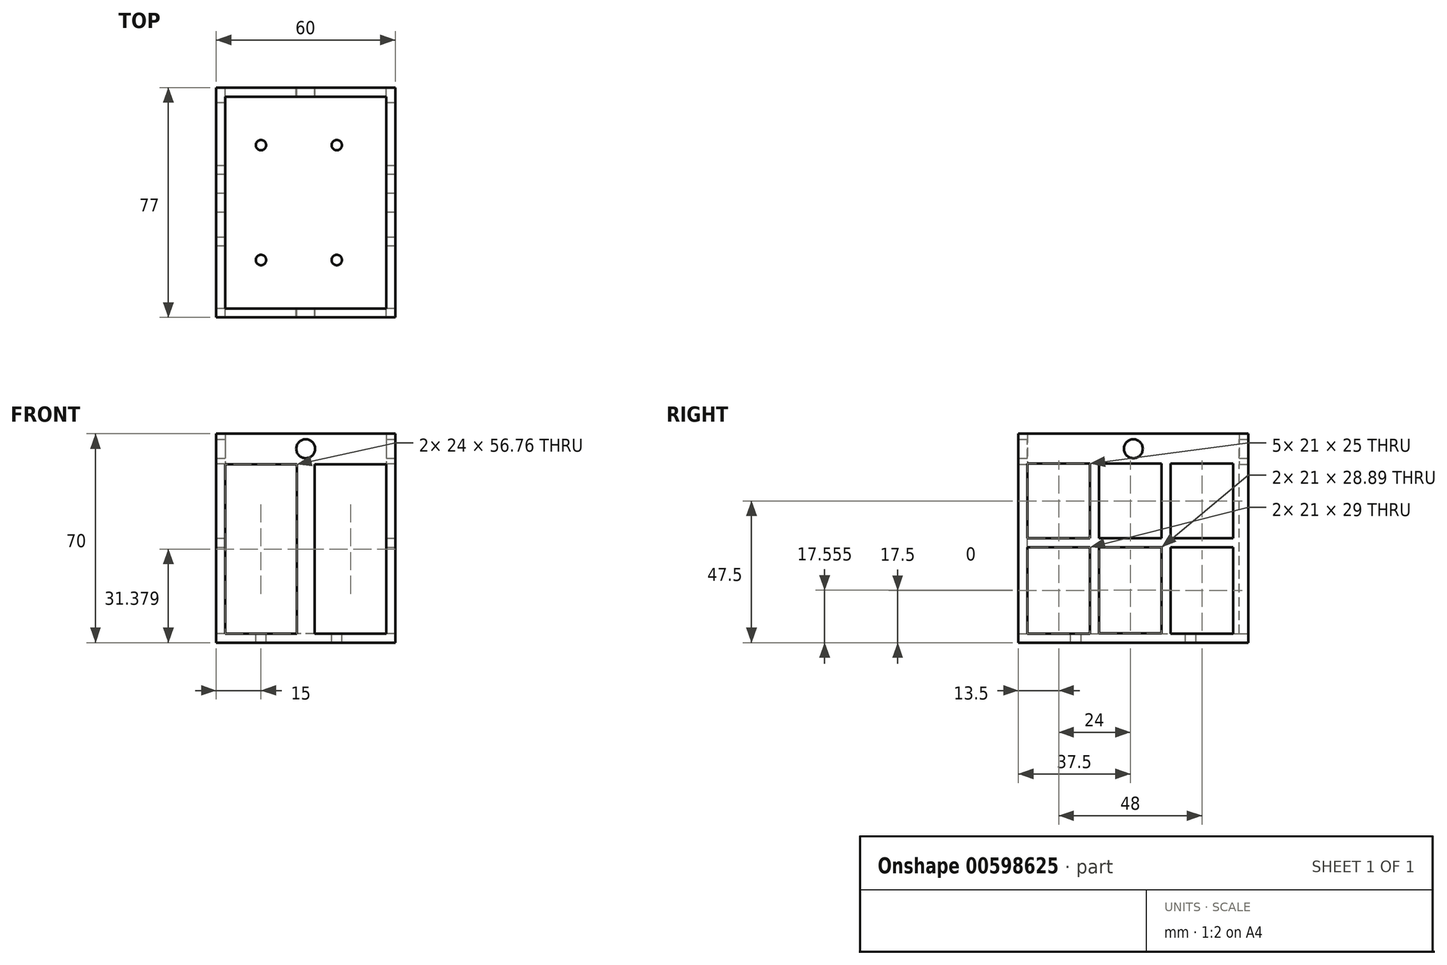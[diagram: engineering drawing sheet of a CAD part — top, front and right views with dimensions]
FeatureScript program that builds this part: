
annotation { "Feature Type Name" : "Feature", "Feature Type Description" : "" }
export const myFeature = defineFeature(function(context is Context, id is Id, definition is map)
    precondition{}
    {
        {
            var Q0;
            Q0=qCreatedBy(makeId("Top.planeOp"),FACE);
            var sketch = newSketch(context, id + "F0", { "sketchPlane" : qUnion([Q0])});
            skLineSegment(sketch, "E0.bottom", {"start": v(30, -38.5) * mm, "end": v(-30, -38.5) * mm});
            skLineSegment(sketch, "E0.top", {"start": v(30, 38.5) * mm, "end": v(-30, 38.5) * mm});
            skLineSegment(sketch, "E0.left", {"start": v(30, -38.5) * mm, "end": v(30, 38.5) * mm});
            skLineSegment(sketch, "E0.right", {"start": v(-30, -38.5) * mm, "end": v(-30, 38.5) * mm});
            skPoint(sketch, "E0.middle", {"position": v(0, 0) * mm});
            skSolve(sketch);
        }
        {
            var Q0;
            Q0=makeQuery(id+"F0.imprint","IMPRINT",FACE,{"disambiguationData":[TD([[makeQuery(id+"F0.imprint","IMPRINT",EDGE,{"derivedFrom":sQuery(id+"F0.wireOp",EDGE,"E0.bottom")}),-1.0]])]});
            extrude(context, id + "F1", {"entities" : qUnion([Q0]), "depth" : 70 * mm, "offsetDistance" : 25.4 * mm});
        }
        {
            var Q0;
            Q0=makeQuery(id+"F1.opExtrude","CAP_FACE",FACE,{"disambiguationData":[OSD([sQuery(id+"F0.wireOp",EDGE,"E0.bottom"),sQuery(id+"F0.wireOp",EDGE,"E0.top"),sQuery(id+"F0.wireOp",EDGE,"E0.left"),sQuery(id+"F0.wireOp",EDGE,"E0.right")])],"isStart":false});
            shell(context, id + "F2", {"entities" : qUnion([Q0]), "thickness" : 3 * mm});
        }
        {
            var Q0;
            Q0=makeQuery(id+"F1.opExtrude","SWEPT_FACE",FACE,{"disambiguationData":[OSD([sQuery(id+"F0.wireOp",EDGE,"E0.left")])]});
            var sketch = newSketch(context, id + "F3", { "sketchPlane" : qUnion([Q0])});
            skLineSegment(sketch, "E1.left", {"start": v(-35.5, 60) * mm, "end": v(-35.5, 35) * mm});
            skLineSegment(sketch, "E2.0", {"start": v(-38.5, 70) * mm, "end": v(38.5, 70) * mm});
            skLineSegment(sketch, "E3.0", {"start": v(-38.5, 70) * mm, "end": v(-38.5, 0) * mm});
            skLineSegment(sketch, "E4.0", {"start": v(38.5, 70) * mm, "end": v(38.5, 0) * mm});
            skLineSegment(sketch, "E5.left", {"start": v(-35.5, 32) * mm, "end": v(-35.5, 3) * mm});
            skCircle(sketch, "E6", {"center": v(0, 65) * mm, "radius": 3.18 * mm});
            skPoint(sketch, "E6.centerSnap0", {"position": v(0, 70) * mm});
            skLineSegment(sketch, "E7", {"start": v(-35.5, 60) * mm, "end": v(-14.5, 60) * mm});
            skLineSegment(sketch, "E8", {"start": v(-14.5, 60) * mm, "end": v(-14.5, 35) * mm});
            skLineSegment(sketch, "E9", {"start": v(-14.5, 35) * mm, "end": v(-35.5, 35) * mm});
            skLineSegment(sketch, "E10.bottom", {"start": v(-11.5, 60) * mm, "end": v(9.5, 60) * mm});
            skLineSegment(sketch, "E10.top", {"start": v(-11.5, 35) * mm, "end": v(9.5, 35) * mm});
            skLineSegment(sketch, "E10.left", {"start": v(-11.5, 60) * mm, "end": v(-11.5, 35) * mm});
            skLineSegment(sketch, "E10.right", {"start": v(9.5, 60) * mm, "end": v(9.5, 35) * mm});
            skLineSegment(sketch, "E11.bottom", {"start": v(12.5, 60) * mm, "end": v(33.5, 60) * mm});
            skLineSegment(sketch, "E11.top", {"start": v(12.5, 35) * mm, "end": v(33.5, 35) * mm});
            skLineSegment(sketch, "E11.left", {"start": v(12.5, 60) * mm, "end": v(12.5, 35) * mm});
            skLineSegment(sketch, "E11.right", {"start": v(33.5, 60) * mm, "end": v(33.5, 35) * mm});
            skLineSegment(sketch, "E12", {"start": v(-35.5, 32) * mm, "end": v(-14.5, 32) * mm});
            skLineSegment(sketch, "E13", {"start": v(-14.5, 32) * mm, "end": v(-14.5, 3) * mm});
            skLineSegment(sketch, "E14", {"start": v(-14.5, 3) * mm, "end": v(-35.5, 3) * mm});
            skLineSegment(sketch, "E15.bottom", {"start": v(-11.5, 32) * mm, "end": v(9.5, 32) * mm});
            skLineSegment(sketch, "E15.top", {"start": v(-11.5, 3.11) * mm, "end": v(9.5, 3.11) * mm});
            skLineSegment(sketch, "E15.left", {"start": v(-11.5, 32) * mm, "end": v(-11.5, 3.11) * mm});
            skLineSegment(sketch, "E15.right", {"start": v(9.5, 32) * mm, "end": v(9.5, 3.11) * mm});
            skPoint(sketch, "E16.oppositeSnap0", {"position": v(-25, 3) * mm});
            skLineSegment(sketch, "E16.bottom", {"start": v(12.5, 32) * mm, "end": v(33.5, 32) * mm});
            skLineSegment(sketch, "E16.top", {"start": v(12.5, 3) * mm, "end": v(33.5, 3) * mm});
            skLineSegment(sketch, "E16.left", {"start": v(12.5, 32) * mm, "end": v(12.5, 3) * mm});
            skLineSegment(sketch, "E16.right", {"start": v(33.5, 32) * mm, "end": v(33.5, 3) * mm});
            skSolve(sketch);
        }
        {
            var Q0;
            Q0=makeQuery(id+"F3.imprint","IMPRINT",FACE,{"disambiguationData":[TD([[makeQuery(id+"F3.imprint","IMPRINT",EDGE,{"derivedFrom":sQuery(id+"F3.wireOp",EDGE,"E1.bottom")}),-1.0]])]});
            var Q1;
            Q1=makeQuery(id+"F3.imprint","IMPRINT",FACE,{"disambiguationData":[TD([[makeQuery(id+"F3.imprint","IMPRINT",EDGE,{"derivedFrom":sQuery(id+"F3.wireOp",EDGE,"7c4a7869-6593-47a0-92b5-f3390c8ad75b.1.0.0")}),1.0]])]});
            var Q2;
            Q2=makeQuery(id+"F3.imprint","IMPRINT",FACE,{"disambiguationData":[TD([[makeQuery(id+"F3.imprint","IMPRINT",EDGE,{"derivedFrom":sQuery(id+"F3.wireOp",EDGE,"E1.left")}),1.0]])]});
            var Q3;
            Q3=makeQuery(id+"F3.imprint","IMPRINT",FACE,{"disambiguationData":[TD([[makeQuery(id+"F3.imprint","IMPRINT",EDGE,{"derivedFrom":sQuery(id+"F3.wireOp",EDGE,"E10.bottom")}),-1.0]])]});
            var Q4;
            Q4=makeQuery(id+"F3.imprint","IMPRINT",FACE,{"disambiguationData":[TD([[makeQuery(id+"F3.imprint","IMPRINT",EDGE,{"derivedFrom":sQuery(id+"F3.wireOp",EDGE,"E11.bottom")}),-1.0]])]});
            var Q5;
            Q5=makeQuery(id+"F3.imprint","IMPRINT",FACE,{"disambiguationData":[TD([[makeQuery(id+"F3.imprint","IMPRINT",EDGE,{"derivedFrom":sQuery(id+"F3.wireOp",EDGE,"E5.left")}),1.0]])]});
            var Q6;
            Q6=makeQuery(id+"F3.imprint","IMPRINT",FACE,{"disambiguationData":[TD([[makeQuery(id+"F3.imprint","IMPRINT",EDGE,{"derivedFrom":sQuery(id+"F3.wireOp",EDGE,"E15.bottom")}),-1.0]])]});
            var Q7;
            Q7=makeQuery(id+"F3.imprint","IMPRINT",FACE,{"disambiguationData":[TD([[makeQuery(id+"F3.imprint","IMPRINT",EDGE,{"derivedFrom":sQuery(id+"F3.wireOp",EDGE,"E16.bottom")}),-1.0]])]});
            extrude(context, id + "F4", {"entities" : qUnion([Q0, Q1, Q2, Q3, Q4, Q5, Q6, Q7]), "operationType" : NewBodyOperationType.REMOVE, "endBound" : BoundingType.THROUGH_ALL, "oppositeDirection" : true, "depth" : 25.4 * mm, "offsetDistance" : 25.4 * mm});
        }
        {
            var Q0;
            Q0=makeQuery(id+"F2.opShell","OFFSET_FACE",FACE,{"disambiguationData":[OSD([sQuery(id+"F0.wireOp",EDGE,"E0.bottom"),sQuery(id+"F0.wireOp",EDGE,"E0.top"),sQuery(id+"F0.wireOp",EDGE,"E0.left"),sQuery(id+"F0.wireOp",EDGE,"E0.right")])]});
            var sketch = newSketch(context, id + "F5", { "sketchPlane" : qUnion([Q0])});
            skPoint(sketch, "E17.0", {"position": v(-30, -38.5) * mm});
            skLineSegment(sketch, "E18", {"start": v(-30, -38.5) * mm, "end": v(0, 0) * mm, "construction": true});
            skPoint(sketch, "E19.0", {"position": v(-30, 0) * mm});
            skPoint(sketch, "E20.0", {"position": v(0, -38.5) * mm});
            skLineSegment(sketch, "E21", {"start": v(-30, 0) * mm, "end": v(0, -38.5) * mm, "construction": true});
            skCircle(sketch, "E22", {"center": v(-15, -19.25) * mm, "radius": 1.75 * mm});
            skCircle(sketch, "E23.0.1.0", {"center": v(-15, 19.25) * mm, "radius": 1.75 * mm});
            skCircle(sketch, "E23.1.0.0", {"center": v(10.4, -19.25) * mm, "radius": 1.75 * mm});
            skCircle(sketch, "E23.1.1.0", {"center": v(10.4, 19.25) * mm, "radius": 1.75 * mm});
            skLineSegment(sketch, "E23.direction1", {"start": v(-15, -19.25) * mm, "end": v(10.4, -19.25) * mm, "construction": true});
            skLineSegment(sketch, "E23.direction2", {"start": v(-15, -19.25) * mm, "end": v(-15, 19.25) * mm, "construction": true});
            skSolve(sketch);
        }
        {
            var Q0;
            Q0=makeQuery(id+"F5.imprint","IMPRINT",FACE,{"disambiguationData":[TD([[makeQuery(id+"F5.imprint","IMPRINT",EDGE,{"derivedFrom":sQuery(id+"F5.wireOp",EDGE,"E22")}),1.0]])]});
            var Q1;
            Q1=makeQuery(id+"F5.imprint","IMPRINT",FACE,{"disambiguationData":[TD([[makeQuery(id+"F5.imprint","IMPRINT",EDGE,{"derivedFrom":sQuery(id+"F5.wireOp",EDGE,"E23.1.0.0")}),1.0]])]});
            var Q2;
            Q2=makeQuery(id+"F5.imprint","IMPRINT",FACE,{"disambiguationData":[TD([[makeQuery(id+"F5.imprint","IMPRINT",EDGE,{"derivedFrom":sQuery(id+"F5.wireOp",EDGE,"E23.0.1.0")}),1.0]])]});
            var Q3;
            Q3=makeQuery(id+"F5.imprint","IMPRINT",FACE,{"disambiguationData":[TD([[makeQuery(id+"F5.imprint","IMPRINT",EDGE,{"derivedFrom":sQuery(id+"F5.wireOp",EDGE,"E23.1.1.0")}),1.0]])]});
            extrude(context, id + "F6", {"entities" : qUnion([Q0, Q1, Q2, Q3]), "operationType" : NewBodyOperationType.REMOVE, "endBound" : BoundingType.THROUGH_ALL, "oppositeDirection" : true, "depth" : 25 * mm, "offsetDistance" : 25 * mm});
        }
        {
            var Q0;
            Q0=makeQuery(id+"F3.imprint","IMPRINT",FACE,{"disambiguationData":[TD([[makeQuery(id+"F3.imprint","IMPRINT",EDGE,{"derivedFrom":sQuery(id+"F3.wireOp",EDGE,"E5.bottom")}),-1.0]])]});
            var Q1;
            Q1=makeQuery(id+"F3.imprint","IMPRINT",FACE,{"disambiguationData":[TD([[makeQuery(id+"F3.imprint","IMPRINT",EDGE,{"derivedFrom":sQuery(id+"F3.wireOp",EDGE,"E6")}),1.0]])]});
            extrude(context, id + "F7", {"entities" : qUnion([Q0, Q1]), "operationType" : NewBodyOperationType.REMOVE, "endBound" : BoundingType.THROUGH_ALL, "oppositeDirection" : true, "depth" : 25 * mm, "offsetDistance" : 25 * mm});
        }
        {
            var Q0;
            Q0=makeQuery(id+"F1.opExtrude","SWEPT_FACE",FACE,{"disambiguationData":[OSD([sQuery(id+"F0.wireOp",EDGE,"E0.top")])]});
            var sketch = newSketch(context, id + "F8", { "sketchPlane" : qUnion([Q0])});
            skCircle(sketch, "E24", {"center": v(0, 65) * mm, "radius": 3.18 * mm});
            skPoint(sketch, "E24.centerSnap0", {"position": v(0, 70) * mm});
            skLineSegment(sketch, "E25.bottom", {"start": v(-27, 59.76) * mm, "end": v(-3, 59.76) * mm});
            skLineSegment(sketch, "E25.top", {"start": v(-27, 3) * mm, "end": v(-3, 3) * mm});
            skLineSegment(sketch, "E25.left", {"start": v(-27, 59.76) * mm, "end": v(-27, 3) * mm});
            skLineSegment(sketch, "E25.right", {"start": v(-3, 59.76) * mm, "end": v(-3, 3) * mm});
            skLineSegment(sketch, "E26.bottom", {"start": v(3, 59.76) * mm, "end": v(27, 59.76) * mm});
            skLineSegment(sketch, "E26.top", {"start": v(3, 3) * mm, "end": v(27, 3) * mm});
            skLineSegment(sketch, "E26.left", {"start": v(3, 59.76) * mm, "end": v(3, 3) * mm});
            skLineSegment(sketch, "E26.right", {"start": v(27, 59.76) * mm, "end": v(27, 3) * mm});
            skSolve(sketch);
        }
        {
            var Q0;
            Q0 = qSketchRegion(id + "F8", true);
            extrude(context, id + "F9", {"entities" : qUnion([Q0]), "operationType" : NewBodyOperationType.REMOVE, "endBound" : BoundingType.THROUGH_ALL, "oppositeDirection" : true, "depth" : 25 * mm, "offsetDistance" : 25 * mm});
        }
        {
            var Q0;
            Q0 = qSketchRegion(id + "F8", true);
            extrude(context, id + "F10", {"entities" : qUnion([Q0]), "operationType" : NewBodyOperationType.REMOVE, "endBound" : BoundingType.THROUGH_ALL, "oppositeDirection" : true, "depth" : 25 * mm, "offsetDistance" : 25 * mm});
        }
    });
